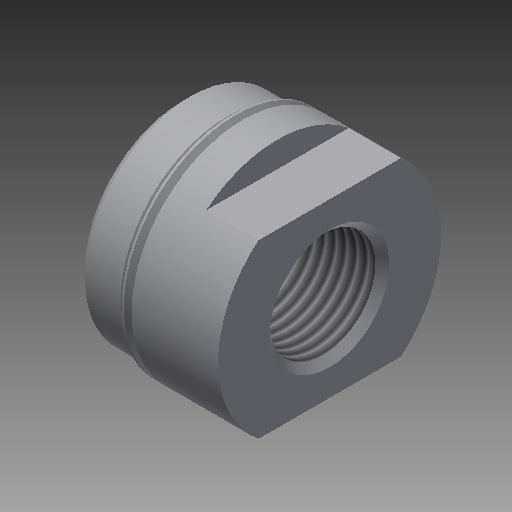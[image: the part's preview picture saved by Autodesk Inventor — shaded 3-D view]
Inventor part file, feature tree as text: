
AUTODESK INVENTOR PART (.ipt)
format: ipt  version: 2018.3 (Build 223284000, 284)  size: 254,976 bytes
history: native  units: in
note: dims shown in document units (in); Inventor stores cm internally (conversion verified against a paired STEP export)
features: other x112, sketch x4, revolve x3, thread x1, extrude x1
ambient origin geometry x8: Origin, YZ Plane, XZ Plane, XY Plane, X Axis, Y Axis, Z Axis, Center Point
bodies: Solid1 (feature_tree)
feature tree (121):
  revolve  "Revolution1"  Angle=360.0deg
  revolve  "Revolution2"  [1 undecoded]
  thread  "Thread1"  [1 undecoded]
  extrude  "Extrusion1"  [1 undecoded]
  revolve  "Revolution3"  [1 undecoded]
  other  "cut1_XY"
  other  "cut1_YZ"
  other  "cut1_ZX"
  other  "cut1_X"
  other  "cut1_Y"
  other  "cut1_Z"
  other  "cut1_Center"
  other  "cut2_XY"
  other  "cut2_YZ"
  other  "cut2_ZX"
  other  "cut2_X"
  other  "cut2_Y"
  other  "cut2_Z"
  other  "cut2_Center"
  other  "cutf1_XY"
  other  "cutf1_YZ"
  other  "cutf1_ZX"
  other  "cutf1_X"
  other  "cutf1_Y"
  other  "cutf1_Z"
  other  "cutf1_Center"
  other  "cutf2_XY"
  other  "cutf2_YZ"
  other  "cutf2_ZX"
  other  "cutf2_X"
  other  "cutf2_Y"
  other  "cutf2_Z"
  other  "cutf2_Center"
  other  "lovra_XY"
  other  "lovra_YZ"
  other  "lovra_ZX"
  other  "lovra_X"
  other  "lovra_Y"
  other  "lovra_Z"
  other  "lovra_Center"
  other  "lovra1_XY"
  other  "lovra1_YZ"
  other  "lovra1_ZX"
  other  "lovra1_X"
  other  "lovra1_Y"
  other  "lovra1_Z"
  other  "lovra1_Center"
  other  "lovra2_XY"
  other  "lovra2_YZ"
  other  "lovra2_ZX"
  other  "lovra2_X"
  other  "lovra2_Y"
  other  "lovra2_Z"
  other  "lovra2_Center"
  other  "lovra21_XY"
  other  "lovra21_YZ"
  other  "lovra21_ZX"
  other  "lovra21_X"
  other  "lovra21_Y"
  other  "lovra21_Z"
  other  "lovra21_Center"
  other  "lovra22_XY"
  other  "lovra22_YZ"
  other  "lovra22_ZX"
  other  "lovra22_X"
  other  "lovra22_Y"
  other  "lovra22_Z"
  other  "lovra22_Center"
  other  "lovra3_XY"
  other  "lovra3_YZ"
  other  "lovra3_ZX"
  other  "lovra3_X"
  other  "lovra3_Y"
  other  "lovra3_Z"
  other  "lovra3_Center"
  other  "olen_XY"
  other  "olen_YZ"
  other  "olen_ZX"
  other  "olen_X"
  other  "olen_Y"
  other  "olen_Z"
  other  "olen_Center"
  other  "to_mounting_bracket_XY"
  other  "to_mounting_bracket_YZ"
  other  "to_mounting_bracket_ZX"
  other  "to_mounting_bracket_X"
  other  "to_mounting_bracket_Y"
  other  "to_mounting_bracket_Z"
  other  "to_mounting_bracket_Center"
  other  "to_nut_XY"
  other  "to_nut_YZ"
  other  "to_nut_ZX"
  other  "to_nut_X"
  other  "to_nut_Y"
  other  "to_nut_Z"
  other  "to_nut_Center"
  other  "to_pin_XY"
  other  "to_pin_YZ"
  other  "to_pin_ZX"
  other  "to_pin_X"
  other  "to_pin_Y"
  other  "to_pin_Z"
  other  "to_pin_Center"
  other  "to_screw_XY"
  other  "to_screw_YZ"
  other  "to_screw_ZX"
  other  "to_screw_X"
  other  "to_screw_Y"
  other  "to_screw_Z"
  other  "to_screw_Center"
  other  "to_tube_XY"
  other  "to_tube_YZ"
  other  "to_tube_ZX"
  other  "to_tube_X"
  other  "to_tube_Y"
  other  "to_tube_Z"
  other  "to_tube_Center"
  sketch  "Sketch_1"  dims[d0=360.0deg d1=360.0deg]
  sketch  "Sketch_6"  dims[d7=0.0in d8=0.0in d9=0.0in d10=0.0in d11=0.0in d12=0.0in d13=0.0in d14=0.0in d15=0.0in d16=0.0in]
  sketch  "Sketch_5"  dims[d2=0.2771in d3=0.0in d4=0.188in d5=0.0in d6=360.0deg]
  sketch  "Sketch_24"
note: 4 required parameter values undecoded (feature->parameter linkage not recoverable at this tier; creation-order binding heuristic only, values carry confidence <= 0.55)